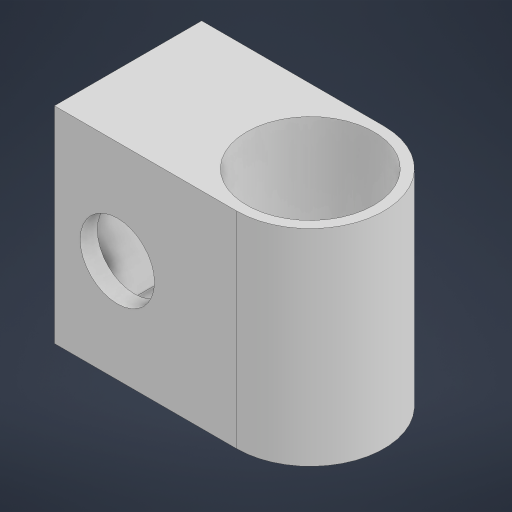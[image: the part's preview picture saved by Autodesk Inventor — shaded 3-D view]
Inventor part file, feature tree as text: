
AUTODESK INVENTOR PART (.ipt)
format: ipt  version: 2023 (Build 270158000, 158)  size: 189,440 bytes
history: native  units: mm
features: extrude x4, sketch x4
ambient origin geometry x8: Origin, YZ Plane, XZ Plane, XY Plane, X Axis, Y Axis, Z Axis, Center Point
bodies: Solid1 (feature_tree)
feature tree (8):
  extrude  "Extrusion1"  Depth=25.75mm
  extrude  "Extrusion2"  Depth=3.0mm
  extrude  "Extrusion3"  Depth=3.0mm
  extrude  "Extrusion4"  Depth=3.0mm TaperAngle=0.0deg
  sketch  "Sketch1"  dims[d0=22.25mm d1=25.75mm]
  sketch  "Sketch2"  dims[d2=36.0mm d3=0.0mm d4=3.0mm]
  sketch  "Sketch3"  dims[d5=3.0mm d6=3.0mm]
  sketch  "Sketch4"  dims[d7=16.0mm d8=0.0mm d9=3.0mm d10=0.0mm d11=13.0mm d12=3.0mm d13=0.0mm]
